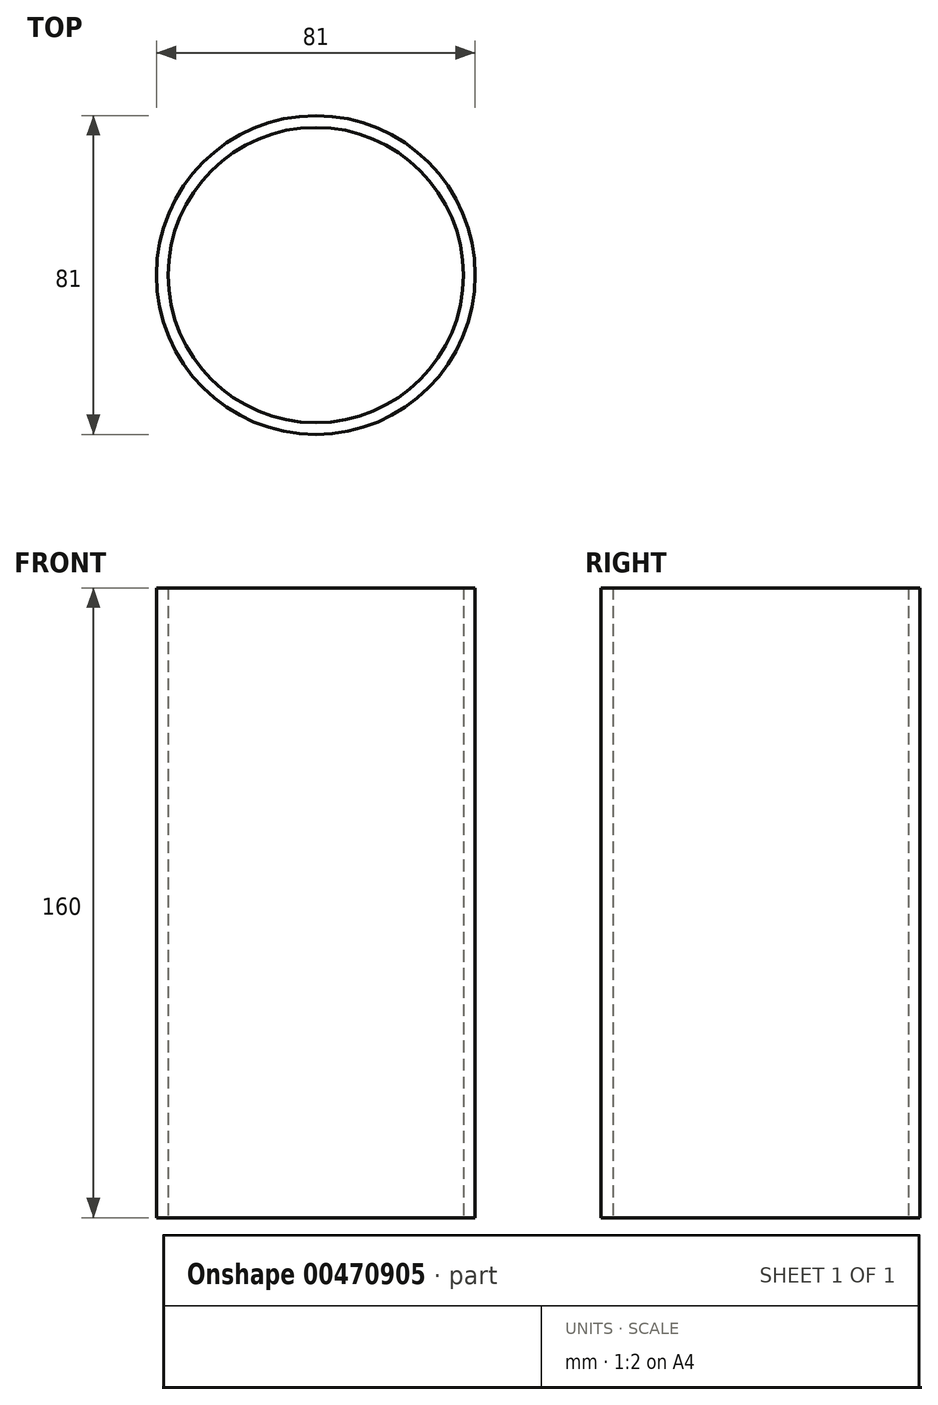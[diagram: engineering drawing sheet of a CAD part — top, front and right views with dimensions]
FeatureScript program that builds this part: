
annotation { "Feature Type Name" : "Feature", "Feature Type Description" : "" }
export const myFeature = defineFeature(function(context is Context, id is Id, definition is map)
    precondition{}
    {
        {
            var Q0;
            Q0=qCreatedBy(makeId("Top.planeOp"),FACE);
            var sketch = newSketch(context, id + "F0", { "sketchPlane" : qUnion([Q0])});
            skCircle(sketch, "E0", {"center": v(0, 0) * mm, "radius": 40.5 * mm});
            skCircle(sketch, "E1", {"center": v(0, 0) * mm, "radius": 37.5 * mm});
            skSolve(sketch);
        }
        {
            var Q0;
            Q0=makeQuery(id+"F0.imprint","IMPRINT",FACE,{"disambiguationData":[TD([[makeQuery(id+"F0.imprint","IMPRINT",EDGE,{"derivedFrom":sQuery(id+"F0.wireOp",EDGE,"E0")}),1.0]])]});
            extrude(context, id + "F1", {"entities" : qUnion([Q0]), "depth" : 160 * mm});
        }
    });
